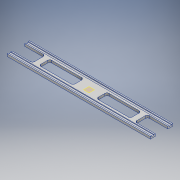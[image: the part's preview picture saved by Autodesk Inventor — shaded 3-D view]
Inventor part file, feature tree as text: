
AUTODESK INVENTOR PART (.ipt)
format: ipt  version: 2017 (Build 210142000, 142)  size: 1,504,768 bytes
history: native  units: mm
features: sketch x2, plane x1, extrude x1, emboss x1
ambient origin geometry x8: Origin, YZ Plane, XZ Plane, XY Plane, X Axis, Y Axis, Z Axis, Center Point
bodies: Body1 (feature_tree)
feature tree (5):
  sketch  "Sketch1"  dims[d0=135.4582mm d1=43.104285mm d4=21.585333mm d5=92.185791mm d8=8.0mm]
  plane  "Work Plane7"
  extrude  "Extrusion6"  Depth=8.0mm
  emboss  "Emboss7"
  sketch  "Sketch7"  dims[d9=8.0mm d10=8.0mm d50=50.779945mm d62=88.879945mm d63=19.05mm d64=50.779945mm d96=9.525mm d97=0.0mm d98=9.525mm d99=4.7625mm d100=4.7625mm d101=9.525mm d102=3.0mm d103=0.0mm]
